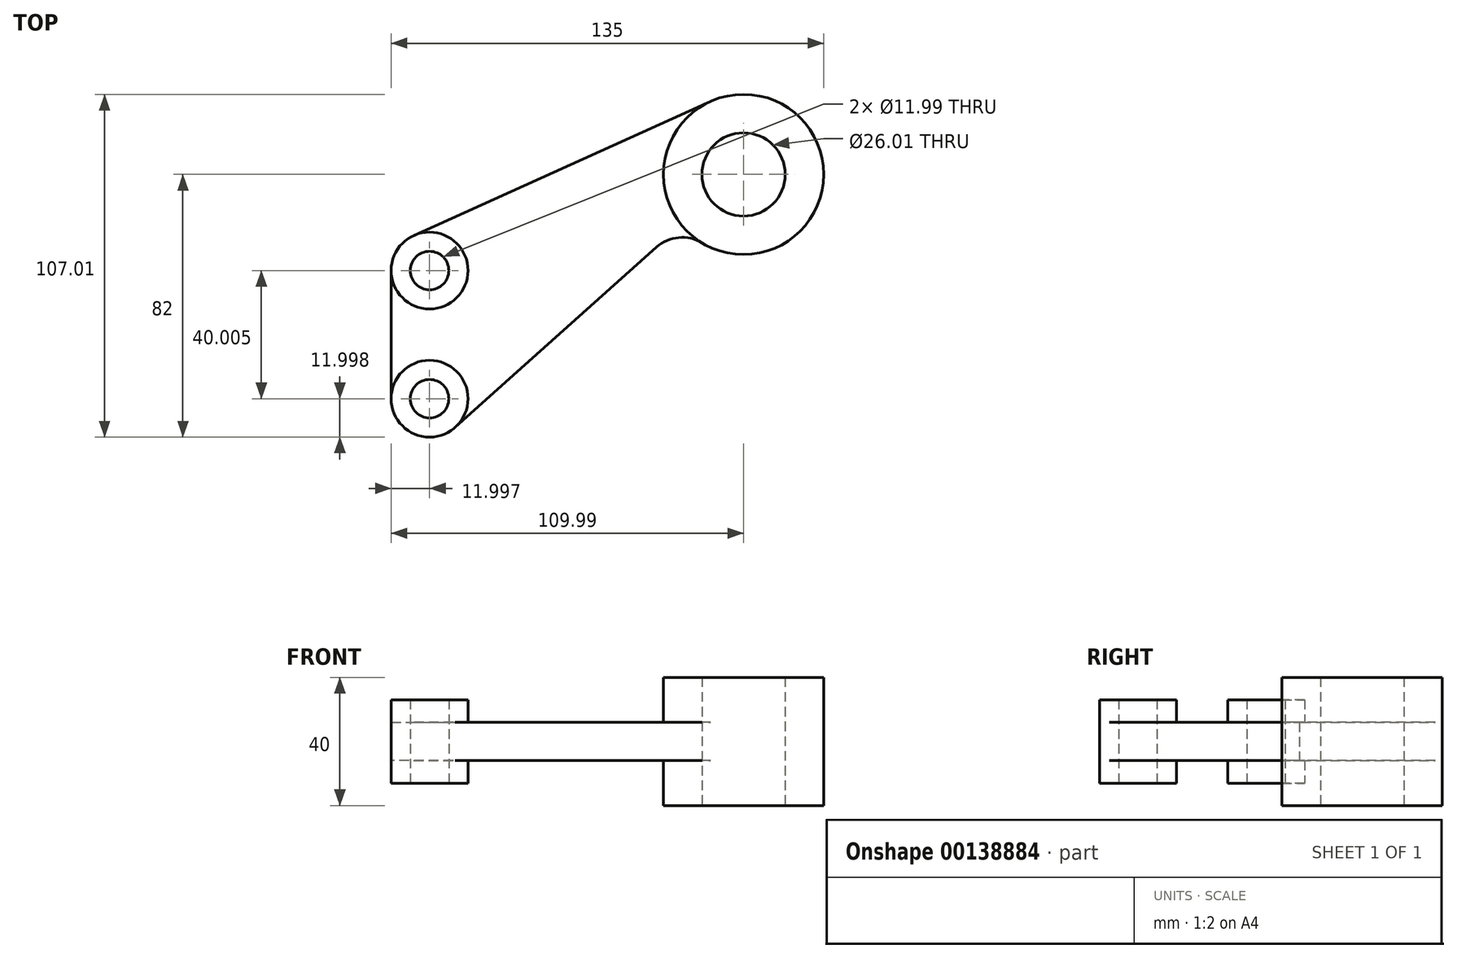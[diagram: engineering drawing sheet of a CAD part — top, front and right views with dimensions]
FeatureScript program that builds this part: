
annotation { "Feature Type Name" : "Feature", "Feature Type Description" : "" }
export const myFeature = defineFeature(function(context is Context, id is Id, definition is map)
    precondition{}
    {
        {
            var Q0;
            Q0=qCreatedBy(makeId("Top.planeOp"),FACE);
            var sketch = newSketch(context, id + "F0", { "sketchPlane" : qUnion([Q0])});
            skCircle(sketch, "E0", {"center": v(0, 0) * mm, "radius": 13 * mm});
            skCircle(sketch, "E1", {"center": v(0, 0) * mm, "radius": 25 * mm});
            skCircle(sketch, "E2", {"center": v(-98, -70) * mm, "radius": 6 * mm});
            skCircle(sketch, "E3", {"center": v(-98, -70) * mm, "radius": 12 * mm});
            skCircle(sketch, "E4", {"center": v(-98, -30) * mm, "radius": 6 * mm});
            skCircle(sketch, "E5", {"center": v(-98, -30) * mm, "radius": 12 * mm});
            skLineSegment(sketch, "E6", {"start": v(-102.93, -19.06) * mm, "end": v(-10.3, 22.79) * mm});
            skLineSegment(sketch, "E7", {"start": v(-110, -30) * mm, "end": v(-110, -70) * mm});
            skArc(sketch, "E8", {"start": v(-12.95, -21.4) * mm, "mid": v(-20.27, -19.71) * mm, "end": v(-27.15, -22.71) * mm});
            skLineSegment(sketch, "E9", {"start": v(-27.15, -22.71) * mm, "end": v(-90, -78.95) * mm});
            skSolve(sketch);
        }
        {
            var Q0;
            Q0=makeQuery(id+"F0.imprint","IMPRINT",FACE,{"disambiguationData":[TD([[makeQuery(id+"F0.imprint","IMPRINT",EDGE,{"derivedFrom":sQuery(id+"F0.wireOp",EDGE,"E0")}),-1.0]])]});
            extrude(context, id + "F1", {"entities" : qUnion([Q0]), "endBound" : BoundingType.SYMMETRIC, "depth" : 40 * mm});
        }
        {
            var Q0;
            {var subQ0=sQuery(id+"F0.wireOp",EDGE,"E6");Q0=makeQuery(id+"F0.imprint","IMPRINT",FACE,{"disambiguationData":[TD([[makeQuery(id+"F0.imprint","IMPRINT",EDGE,{"derivedFrom":subQ0}),-1.0]])]});}
            extrude(context, id + "F2", {"entities" : qUnion([Q0]), "operationType" : NewBodyOperationType.ADD, "endBound" : BoundingType.SYMMETRIC, "depth" : 12 * mm});
        }
        {
            var Q0;
            Q0=makeQuery(id+"F0.imprint","IMPRINT",FACE,{"disambiguationData":[TD([[makeQuery(id+"F0.imprint","IMPRINT",EDGE,{"derivedFrom":sQuery(id+"F0.wireOp",EDGE,"E4")}),-1.0]])]});
            var Q1;
            Q1=makeQuery(id+"F0.imprint","IMPRINT",FACE,{"disambiguationData":[TD([[makeQuery(id+"F0.imprint","IMPRINT",EDGE,{"derivedFrom":sQuery(id+"F0.wireOp",EDGE,"E2")}),-1.0]])]});
            extrude(context, id + "F3", {"entities" : qUnion([Q0, Q1]), "operationType" : NewBodyOperationType.ADD, "endBound" : BoundingType.SYMMETRIC, "depth" : 26 * mm});
        }
    });
